FREECAD ASSEMBLY — COMPONENT RECIPES ("column-motor")

This assembly document has 16 components, labeled P0..P15 below (a component is one placed body or linked part). 3 of them carry a construction recipe — the FreeCAD feature program that regenerates the part from scratch, quoted from this document or its linked companion documents; the rest are supplied as boundary geometry only. No exploded tour is included for this assembly.
COMPONENT P0 — recipe-attached ("Semelle", modeled in this document).
Construction recipe (the document's own serialized feature program — sketch geometry with constraints, then the solid features built on it; lengths are millimeters unless a unit is written):

FEATURE [Sketcher::SketchObject] Sketch032
  ArcFitTolerance = 0
  ExternalBSplineMaxDegree = 0
  ExternalBSplineTolerance = 0
  FixShape = 1
  FullyConstrained = true
  InternalTolerance = 1e-06
  InvalidShape = false
  MakeInternals = false
  MapMode = 5
  TreeRank = 0
  ValidateShape = false
  sketch-geometry (56):
    g0: LineSegment StartX=-126.423 StartY=-21.0289 StartZ=0 EndX=-58.007 EndY=18.4711 EndZ=0
    g1: LineSegment StartX=-58.007 StartY=18.4711 StartZ=0 EndX=-45 EndY=41 EndZ=0
    g2: LineSegment StartX=-45 StartY=41 StartZ=0 EndX=-45 EndY=120 EndZ=0
    g3: LineSegment StartX=-45 StartY=120 StartZ=0 EndX=45 EndY=120 EndZ=0
    g4: LineSegment StartX=45 StartY=120 StartZ=0 EndX=45 EndY=41 EndZ=0
    g5: LineSegment StartX=45 StartY=41 StartZ=0 EndX=58.007 EndY=18.4711 EndZ=0
    g6: LineSegment StartX=58.007 StartY=18.4711 StartZ=0 EndX=126.423 EndY=-21.0289 EndZ=0
    g7: LineSegment StartX=126.423 StartY=-21.0289 StartZ=0 EndX=81.423 EndY=-98.9711 EndZ=0
    g8: LineSegment StartX=81.423 StartY=-98.9711 StartZ=0 EndX=13.007 EndY=-59.4711 EndZ=0
    g9: LineSegment StartX=13.007 StartY=-59.4711 StartZ=0 EndX=-13.007 EndY=-59.4711 EndZ=0
    g10: LineSegment StartX=-13.007 StartY=-59.4711 StartZ=0 EndX=-81.423 EndY=-98.9711 EndZ=0
    g11: LineSegment StartX=-81.423 StartY=-98.9711 StartZ=0 EndX=-126.423 EndY=-21.0289 EndZ=0
    g12: LineSegment [constr] StartX=0 StartY=0 StartZ=0 EndX=0 EndY=120 EndZ=0
    g13: LineSegment [constr] StartX=0 StartY=0 StartZ=0 EndX=-103.923 EndY=-60 EndZ=0
    g14: LineSegment [constr] StartX=0 StartY=0 StartZ=0 EndX=103.923 EndY=-60 EndZ=0
    g15: LineSegment StartX=-27.5 StartY=82 StartZ=0 EndX=27.5 EndY=82 EndZ=0
    g16: LineSegment StartX=27.5 StartY=82 StartZ=0 EndX=27.5 EndY=110 EndZ=0
    g17: LineSegment StartX=27.5 StartY=110 StartZ=0 EndX=-27.5 EndY=110 EndZ=0
    g18: LineSegment StartX=-27.5 StartY=110 StartZ=0 EndX=-27.5 EndY=82 EndZ=0
    g19: LineSegment StartX=57.2641 StartY=-64.8157 StartZ=0 EndX=84.7641 EndY=-17.1843 EndZ=0
    g20: LineSegment StartX=84.7641 StartY=-17.1843 StartZ=0 EndX=109.013 EndY=-31.1843 EndZ=0
    g21: LineSegment StartX=109.013 StartY=-31.1843 StartZ=0 EndX=81.5128 EndY=-78.8157 EndZ=0
    g22: LineSegment StartX=81.5128 StartY=-78.8157 StartZ=0 EndX=57.2641 EndY=-64.8157 EndZ=0
    g23: LineSegment StartX=-109.013 StartY=-31.1843 StartZ=0 EndX=-81.5128 EndY=-78.8157 EndZ=0
    g24: LineSegment StartX=-81.5128 StartY=-78.8157 StartZ=0 EndX=-57.2641 EndY=-64.8157 EndZ=0
    g25: LineSegment StartX=-57.2641 StartY=-64.8157 StartZ=0 EndX=-84.7641 EndY=-17.1843 EndZ=0
    g26: LineSegment StartX=-84.7641 StartY=-17.1843 StartZ=0 EndX=-109.013 EndY=-31.1843 EndZ=0
    g27: Circle [constr] CenterX=0 CenterY=0 CenterZ=0 NormalX=0 NormalY=0 NormalZ=1 AngleXU=0 Radius=86.4884
    g28: LineSegment StartX=-11.547 StartY=-20 StartZ=0 EndX=-23.094 EndY=-3.6e-15 EndZ=0
    g29: LineSegment StartX=-23.094 StartY=-3.3e-15 StartZ=0 EndX=-11.547 EndY=20 EndZ=0
    g30: LineSegment StartX=-11.547 StartY=20 StartZ=0 EndX=11.547 EndY=20 EndZ=0
    g31: LineSegment StartX=11.547 StartY=20 StartZ=0 EndX=23.094 EndY=0 EndZ=0
    g32: LineSegment StartX=23.094 StartY=0 StartZ=0 EndX=11.547 EndY=-20 EndZ=0
    g33: LineSegment StartX=11.547 StartY=-20 StartZ=0 EndX=-11.547 EndY=-20 EndZ=0
    g34: Circle [constr] CenterX=0 CenterY=0 CenterZ=0 NormalX=0 NormalY=0 NormalZ=1 AngleXU=0 Radius=23.094
    g35: Circle CenterX=-21.6506 CenterY=12.5 CenterZ=0 NormalX=0 NormalY=0 NormalZ=1 AngleXU=0 Radius=1.6
    g36: Circle CenterX=21.6506 CenterY=12.5 CenterZ=0 NormalX=0 NormalY=0 NormalZ=1 AngleXU=0 Radius=1.6
    g37: Circle CenterX=0 CenterY=-25 CenterZ=0 NormalX=0 NormalY=0 NormalZ=1 AngleXU=0 Radius=1.6
    g38: LineSegment [constr] StartX=0 StartY=-25 StartZ=0 EndX=0 EndY=0 EndZ=0
    g39: LineSegment [constr] StartX=0 StartY=0 StartZ=0 EndX=21.6506 EndY=12.5 EndZ=0
    g40: LineSegment [constr] StartX=0 StartY=0 StartZ=0 EndX=-21.6506 EndY=12.5 EndZ=0
    g41: LineSegment [constr] StartX=-45 StartY=120 StartZ=0 EndX=-126.423 EndY=-21.0289 EndZ=0
    g42: LineSegment [constr] StartX=-81.423 StartY=-98.9711 StartZ=0 EndX=81.423 EndY=-98.9711 EndZ=0
    g43: LineSegment [constr] StartX=126.423 StartY=-21.0289 StartZ=0 EndX=45 EndY=120 EndZ=0
    g44: LineSegment [constr] StartX=-45 StartY=120 StartZ=0 EndX=-55 EndY=102.679 EndZ=0
    g45: LineSegment [constr] StartX=-55 StartY=102.679 StartZ=0 EndX=-45 EndY=41 EndZ=0
    g46: LineSegment [constr] StartX=-58.007 StartY=18.4711 StartZ=0 EndX=-116.423 EndY=-3.70835 EndZ=0
    g47: LineSegment [constr] StartX=-116.423 StartY=-3.70835 StartZ=0 EndX=-126.423 EndY=-21.0289 EndZ=0
    g48: LineSegment [constr] StartX=-81.423 StartY=-98.9711 StartZ=0 EndX=-61.423 EndY=-98.9711 EndZ=0
    g49: LineSegment [constr] StartX=-61.423 StartY=-98.9711 StartZ=0 EndX=-13.007 EndY=-59.4711 EndZ=0
    g50: LineSegment [constr] StartX=13.007 StartY=-59.4711 StartZ=0 EndX=61.423 EndY=-98.9711 EndZ=0
    g51: LineSegment [constr] StartX=61.423 StartY=-98.9711 StartZ=0 EndX=81.423 EndY=-98.9711 EndZ=0
    g52: LineSegment [constr] StartX=126.423 StartY=-21.0289 StartZ=0 EndX=116.423 EndY=-3.70835 EndZ=0
    g53: LineSegment [constr] StartX=116.423 StartY=-3.70835 StartZ=0 EndX=58.007 EndY=18.4711 EndZ=0
    g54: LineSegment [constr] StartX=45 StartY=41 StartZ=0 EndX=55 EndY=102.679 EndZ=0
    g55: LineSegment [constr] StartX=55 StartY=102.679 StartZ=0 EndX=45 EndY=120 EndZ=0
  constraints (151):
    c: Coincident(g0,g1)
    c: Coincident(g1,g2)
    c: Vertical(g2)
    c: Coincident(g2,g3)
    c: Horizontal(g3)
    c: Coincident(g3,g4)
    c: Vertical(g4)
    c: Coincident(g4,g5)
    c: Coincident(g5,g6)
    c: Coincident(g6,g7)
    c: Coincident(g7,g8)
    c: Coincident(g8,g9)
    c: Horizontal(g9)
    c: Coincident(g9,g10)
    c: Coincident(g10,g11)
    c: Coincident(g11,g0)
    c: Parallel(g8,g6)
    c: Parallel(g10,g0)
    c: Equal(g4,g6)
    c: Equal(g6,g8)
    c: Equal(g8,g10)
    c: Equal(g10,g0)
    c: Equal(g0,g2)
    c: Perpendicular(g6,g7)
    c: Perpendicular(g11,g10)
    c: Coincident(g12,g-1)
    c: PointOnObject(g12,g3)
    c: Vertical(g12)
    c: Coincident(g13,g12)
    c: Coincident(g14,g12)
    c: Symmetric(g6,g7,g14)
    c: Symmetric(g10,g0,g13)
    c: Perpendicular(g13,g11)
    c: Perpendicular(g7,g14)
    c: DistanceX(g3,g3) = 90
    c: Equal(g9,g5)
    c: Equal(g5,g1)
    c: Angle(g14,g12) = 2.0944
    c: Angle(g12,g13) = 2.0944
    c: DistanceY(g12,g2) = 120
    c: DistanceX(g9,g9) = 26.0141
    c: Coincident(g15,g16)
    c: Coincident(g16,g17)
    c: Coincident(g17,g18)
    c: Coincident(g18,g15)
    c: Horizontal(g15)
    c: Vertical(g16)
    c: Vertical(g18)
    c: Symmetric(g16,g17,g12)
    c: DistanceX(g17,g17) = 55
    c: DistanceY(g16,g16) = 28
    c: Coincident(g19,g20)
    c: Coincident(g20,g21)
    c: Coincident(g21,g22)
    c: Coincident(g22,g19)
    c: Coincident(g23,g24)
    c: Coincident(g24,g25)
    c: Coincident(g25,g26)
    c: Coincident(g26,g23)
    c: Equal(g25,g23)
    c: Equal(g23,g19)
    c: Equal(g19,g21)
    c: Equal(g21,g15)
    c: Equal(g22,g20)
    c: Equal(g20,g16)
    c: Equal(g16,g26)
    c: Equal(g26,g24)
    c: Parallel(g24,g13)
    c: Parallel(g22,g14)
    c: Symmetric(g23,g23,g13)
    c: Symmetric(g21,g20,g14)
    c: Coincident(g27,g12)
    c: PointOnObject(g19,g27)
    c: PointOnObject(g24,g27)
    c: PointOnObject(g15,g27)
    c: Equal(g11,g7)
    c: Equal(g7,g3)
    c: Coincident(g28,g29)
    c: Coincident(g29,g30)
    c: Coincident(g30,g31)
    c: Coincident(g31,g32)
    c: Coincident(g32,g33)
    c: Coincident(g33,g28)
    c: Horizontal(g33)
    c: Horizontal(g30)
    c: Equal(g29,g30)
    c: Equal(g30,g31)
    c: Equal(g31,g32)
    c: Equal(g32,g33)
    c: Equal(g33,g28)
    c: Coincident(g34,g12)
    c: PointOnObject(g30,g34)
    c: PointOnObject(g31,g34)
    c: PointOnObject(g32,g34)
    c: PointOnObject(g28,g34)
    c: PointOnObject(g28,g34)
    c: DistanceY(g12,g30) = 20
    c: PointOnObject(g37,g-2)
    c: Equal(g37,g36)
    c: Equal(g36,g35)
    c: Diameter(g35) = 3.2
    c: Coincident(g38,g37)
    c: Coincident(g38,g12)
    c: Coincident(g39,g12)
    c: Coincident(g39,g36)
    c: Coincident(g40,g12)
    c: Coincident(g40,g35)
    c: Perpendicular(g29,g40)
    c: Perpendicular(g31,g39)
    c: Equal(g40,g38)
    c: Equal(g38,g39)
    c: DistanceY(g38,g38) = 25
    c: Coincident(g41,g3)
    c: Coincident(g41,g11)
    c: Coincident(g42,g11)
    c: Coincident(g42,g7)
    c: Coincident(g43,g7)
    c: Coincident(g43,g3)
    c: Coincident(g3,g44)
    c: PointOnObject(g44,g41)
    c: Coincident(g44,g45)
    c: Coincident(g45,g1)
    c: Coincident(g1,g46)
    c: PointOnObject(g46,g41)
    c: Coincident(g46,g47)
    c: Coincident(g47,g11)
    c: Coincident(g11,g48)
    c: Horizontal(g48)
    c: Coincident(g48,g49)
    c: Coincident(g49,g9)
    c: Coincident(g9,g50)
    c: PointOnObject(g50,g42)
    c: Coincident(g50,g51)
    c: Coincident(g51,g7)
    c: Coincident(g7,g52)
    c: PointOnObject(g52,g43)
    c: Coincident(g52,g53)
    c: Coincident(g53,g5)
    c: Coincident(g5,g54)
    c: PointOnObject(g54,g43)
    c: Coincident(g54,g55)
    c: Coincident(g55,g3)
    c: Equal(g55,g44)
    c: Equal(g44,g47)
    c: Equal(g47,g48)
    c: Equal(g48,g51)
    c: Equal(g55,g52)
    c: DistanceX(g48,g48) = 20
    c: DistanceY(g16) = 110
    c: DistanceY(g50,g12) = 98.9711
    c: DistanceY(g4,g4) = 79
FEATURE [PartDesign::Pad] Pad020
  AddSubType = 0
  AutoTaperInnerAngle = true
  CheckUpToFaceLimits = true
  ClaimChildren = false
  Direction = (0,0,1)
  Fit = 0
  FitJoin = 0
  FixShape = 1
  InnerFit = 0
  InnerFitJoin = 0
  InvalidShape = false
  Length = 5
  Length2 = 100
  NewSolid = false
  Profile = -> Sketch032
  Refine = true
  Reversed = true
  Suppress = false
  TaperInnerAngle = 0
  TaperInnerAngleRev = 0
  TreeRank = 0
  Type = 0
  ValidateShape = true
  _ProfileBasedVersion = 0
FEATURE [PartDesign::Fillet] Fillet008
  AddSubType = 0
  Base = -> Pad020 [Edge41,Edge44,Edge37,Edge38,Edge65,Edge62,Edge61,Edge68,Edge49,Edge50,Edge53,Edge56]
  BaseFeature = -> Pad020
  FixShape = 1
  InvalidShape = false
  NewSolid = false
  Radius = 3
  Refine = true
  SupportTransform = false
  Suppress = false
  TreeRank = 0
  UseAllEdges = false
  ValidateShape = true
FEATURE [PartDesign::Fillet] Fillet009
  AddSubType = 0
  Base = -> Fillet008 [Edge110,Edge99,Edge107,Edge106,Edge102,Edge103]
  BaseFeature = -> Fillet008
  FixShape = 1
  InvalidShape = false
  NewSolid = false
  Radius = 5
  Refine = true
  SupportTransform = false
  Suppress = false
  TreeRank = 0
  UseAllEdges = false
  ValidateShape = true
FEATURE [PartDesign::Fillet] Fillet010
  AddSubType = 0
  Base = -> Fillet009 [Edge53,Edge57,Edge67,Edge71,Edge77,Edge81]
  BaseFeature = -> Fillet009
  FixShape = 1
  InvalidShape = false
  NewSolid = false
  Radius = 5
  Refine = true
  SupportTransform = false
  Suppress = false
  TreeRank = 0
  UseAllEdges = false
  ValidateShape = true
FEATURE [Sketcher::SketchObject] Sketch033
  ArcFitTolerance = 0
  ExternalBSplineMaxDegree = 0
  ExternalBSplineTolerance = 0
  FixShape = 1
  FullyConstrained = true
  InternalTolerance = 1e-06
  InvalidShape = false
  MakeInternals = false
  MapMode = 5
  TreeRank = 0
  ValidateShape = false
  sketch-geometry (17):
    g0: Circle CenterX=-20 CenterY=115 CenterZ=0 NormalX=0 NormalY=0 NormalZ=1 AngleXU=0 Radius=1.75
    g1: Circle CenterX=20 CenterY=115 CenterZ=0 NormalX=0 NormalY=0 NormalZ=1 AngleXU=0 Radius=1.75
    g2: Circle CenterX=-35 CenterY=60 CenterZ=0 NormalX=0 NormalY=0 NormalZ=1 AngleXU=0 Radius=1.75
    g3: Circle CenterX=-35 CenterY=100 CenterZ=0 NormalX=0 NormalY=0 NormalZ=1 AngleXU=0 Radius=1.75
    g4: Circle CenterX=35 CenterY=100 CenterZ=0 NormalX=0 NormalY=0 NormalZ=1 AngleXU=0 Radius=1.75
    g5: Circle CenterX=35 CenterY=60 CenterZ=0 NormalX=0 NormalY=0 NormalZ=1 AngleXU=0 Radius=1.75
    g6: Circle CenterX=-35 CenterY=115 CenterZ=0 NormalX=0 NormalY=0 NormalZ=1 AngleXU=0 Radius=3.1
    g7: Circle CenterX=35 CenterY=115 CenterZ=0 NormalX=0 NormalY=0 NormalZ=1 AngleXU=0 Radius=3.1
    g8: Circle CenterX=-35 CenterY=80 CenterZ=0 NormalX=0 NormalY=0 NormalZ=1 AngleXU=0 Radius=2.2
    g9: Circle CenterX=35 CenterY=80 CenterZ=0 NormalX=0 NormalY=0 NormalZ=1 AngleXU=0 Radius=2.2
    g10: Circle CenterX=-35 CenterY=50 CenterZ=0 NormalX=0 NormalY=0 NormalZ=1 AngleXU=0 Radius=2.2
    g11: Circle CenterX=35 CenterY=50 CenterZ=0 NormalX=0 NormalY=0 NormalZ=1 AngleXU=0 Radius=2.2
    g12: Circle CenterX=-1.4e-15 CenterY=115 CenterZ=0 NormalX=0 NormalY=0 NormalZ=1 AngleXU=0 Radius=2.2
    g13: Circle CenterX=-25.75 CenterY=76 CenterZ=0 NormalX=0 NormalY=0 NormalZ=1 AngleXU=0 Radius=1.75
    g14: Circle CenterX=-25.75 CenterY=55 CenterZ=0 NormalX=0 NormalY=0 NormalZ=1 AngleXU=0 Radius=1.75
    g15: Circle CenterX=25.75 CenterY=76 CenterZ=0 NormalX=0 NormalY=0 NormalZ=1 AngleXU=0 Radius=1.75
    g16: Circle CenterX=25.75 CenterY=55 CenterZ=0 NormalX=0 NormalY=0 NormalZ=1 AngleXU=0 Radius=1.75
  constraints (41):
    c: Equal(g0,g3)
    c: Equal(g3,g2)
    c: Equal(g2,g1)
    c: Equal(g1,g4)
    c: Equal(g4,g5)
    c: Diameter(g0) = 3.5
    c: Symmetric(g1,g0,g-2)
    c: Symmetric(g3,g4,g-2)
    c: Symmetric(g2,g5,g-2)
    c: Vertical(g3,g2)
    c: DistanceX(g3,g4) = 70
    c: DistanceX(g0,g1) = 40
    c: DistanceY(g4,g1) = 15
    c: DistanceY(g5,g4) = 40
    c: DistanceY(g-1,g1) = 115
    c: Symmetric(g7,g6,g-2)
    c: Horizontal(g6,g0)
    c: Diameter(g7) = 6.2
    c: Equal(g7,g6)
    c: Vertical(g7,g4)
    c: Equal(g9,g8)
    c: Symmetric(g8,g9,g-2)
    c: Symmetric(g5,g4,g9)
    c: Diameter(g9) = 4.4
    c: Symmetric(g1,g0,g12)
    c: Equal(g12,g11)
    c: Equal(g11,g10)
    c: Equal(g10,g9)
    c: Vertical(g11,g5)
    c: Symmetric(g11,g10,g-2)
    c: DistanceY(g11,g5) = 10
    c: Equal(g15,g16)
    c: Equal(g16,g14)
    c: Equal(g14,g13)
    c: Equal(g13,g2)
    c: Vertical(g13,g14)
    c: Symmetric(g15,g13,g-2)
    c: Symmetric(g14,g16,g-2)
    c: DistanceX(g8,g13) = 9.25
    c: DistanceY(g-1,g13) = 76
    c: DistanceY(g14,g13) = 21
FEATURE [PartDesign::Pocket] Pocket012
  AddSubType = 1
  AutoTaperInnerAngle = true
  BaseFeature = -> Fillet010
  CheckUpToFaceLimits = true
  ClaimChildren = false
  Direction = (0,0,-1)
  Fit = 0
  FitJoin = 0
  FixShape = 1
  InnerFit = 0
  InnerFitJoin = 0
  InvalidShape = false
  Length = 5
  Length2 = 100
  NewSolid = false
  Profile = -> Sketch033
  Refine = true
  Suppress = false
  TaperInnerAngle = 0
  TaperInnerAngleRev = 0
  TreeRank = 0
  Type = 1
  ValidateShape = true
  _ProfileBasedVersion = 0
  _Version = 0
FEATURE [PartDesign::PolarPattern] PolarPattern013
  AddSubType = 0
  Angle = 360
  Axis = -> Sketch033 [N_Axis]
  BaseFeature = -> Pocket012
  CopyShape = true
  FixShape = 1
  HideBaseFeature = false
  InvalidShape = false
  NewSolid = false
  Occurrences = 3
  OffsetBaseFeature = true
  OriginalSubs = -> [Pocket012]
  Originals = -> [Pocket012]
  ParallelTransform = true
  Refine = true
  SubTransform = true
  Suppress = false
  TreeRank = 0
  ValidateShape = true
  _Version = 0
FEATURE [Sketcher::SketchObject] Sketch034
  ArcFitTolerance = 0
  ExternalBSplineMaxDegree = 0
  ExternalBSplineTolerance = 0
  ExternalGeometry = -> [PolarPattern013]
  FixShape = 1
  FullyConstrained = true
  InternalTolerance = 1e-06
  InvalidShape = false
  MakeInternals = false
  MapMode = 5
  TreeRank = 0
  ValidateShape = false
  sketch-geometry (5):
    g0: LineSegment StartX=-21.5 StartY=20 StartZ=0 EndX=21.5 EndY=20 EndZ=0
    g1: LineSegment StartX=21.5 StartY=20 StartZ=0 EndX=21.5 EndY=82 EndZ=0
    g2: LineSegment StartX=21.5 StartY=82 StartZ=0 EndX=-21.5 EndY=82 EndZ=0
    g3: LineSegment StartX=-21.5 StartY=82 StartZ=0 EndX=-21.5 EndY=20 EndZ=0
    g4: GeomPoint [constr] X=0 Y=51 Z=0
  constraints (13):
    c: Coincident(g0,g1)
    c: Coincident(g1,g2)
    c: Coincident(g2,g3)
    c: Coincident(g3,g0)
    c: Horizontal(g0)
    c: Horizontal(g2)
    c: Vertical(g1)
    c: Vertical(g3)
    c: Symmetric(g2,g0,g4)
    c: PointOnObject(g4,g-2)
    c: Distance(g2,g2) = 43
    c: PointOnObject(g-4,g0)
    c: PointOnObject(g1,g-3)
FEATURE [PartDesign::Pocket] Pocket
  AddSubType = 1
  AutoTaperInnerAngle = true
  BaseFeature = -> PolarPattern013
  CheckUpToFaceLimits = true
  ClaimChildren = false
  Direction = (0,0,-1)
  Fit = 0
  FitJoin = 0
  FixShape = 1
  InnerFit = 0
  InnerFitJoin = 0
  InvalidShape = false
  Length = 5
  Length2 = 5
  NewSolid = false
  Profile = -> Sketch034
  ReferenceAxis = -> Sketch034 [N_Axis]
  Refine = true
  Suppress = false
  TaperInnerAngle = 0
  TaperInnerAngleRev = 0
  TreeRank = 0
  Type = 1
  ValidateShape = true
  _ProfileBasedVersion = 0
  _Version = 0
FEATURE [PartDesign::PolarPattern] PolarPattern
  AddSubType = 0
  Angle = 360
  Axis = -> Z_Axis026
  BaseFeature = -> Pocket
  CopyShape = true
  FixShape = 1
  HideBaseFeature = false
  InvalidShape = false
  NewSolid = false
  Occurrences = 3
  OffsetBaseFeature = true
  OriginalSubs = -> [Pocket]
  Originals = -> [Pocket]
  ParallelTransform = true
  Refine = true
  SubTransform = true
  Suppress = false
  TreeRank = 0
  ValidateShape = true
  _Version = 0
FEATURE [PartDesign::Fillet] Fillet011
  AddSubType = 0
  Base = -> PolarPattern [Edge284,Edge302,Edge340,Edge275,Edge312,Edge330,Edge334,Edge336,Edge278,Edge280,Edge306,Edge308]
  BaseFeature = -> PolarPattern
  FixShape = 1
  InvalidShape = false
  NewSolid = false
  Radius = 2
  Refine = true
  SupportTransform = false
  Suppress = false
  TreeRank = 0
  UseAllEdges = false
  ValidateShape = true
FEATURE [PartDesign::Body] Body019  label="Semelle"
  AutoGroupSolids = false
  ClaimAllChildren = false
  ExportMode = 0
  FixShape = 1
  Group = -> [Sketch032,Pad020,Fillet008,Fillet009,Fillet010,Sketch033,Pocket012,PolarPattern013,Sketch034,Pocket,PolarPattern,Fillet011]
  InvalidShape = false
  Origin = -> Origin029
  SingleSolid = true
  Tip = -> Fillet011
  TreeRank = 0
  ValidateShape = false
  _ExportChildren = -> [Pad020,Fillet008,Fillet009,Fillet010,Pocket012,PolarPattern013,Pocket,PolarPattern,Fillet011]
  _GroupVersion = 1
COMPONENT P1 — recipe-attached ("Side_A", modeled in this document).
Construction recipe (the document's own serialized feature program — sketch geometry with constraints, then the solid features built on it; lengths are millimeters unless a unit is written):

FEATURE [Sketcher::SketchObject] Sketch136
  ArcFitTolerance = 1e-06
  AttachmentSupport = -> [YZ_Plane085]
  ExternalBSplineMaxDegree = 5
  ExternalBSplineTolerance = 0.0001
  FullyConstrained = true
  InternalTolerance = 1e-06
  InvalidShape = false
  MakeInternals = false
  MapMode = 5
  Placement = pos=(0,0,0) rot=(0.57735,0.57735,0.57735;2.0944rad)
  Support = -> [YZ_Plane085]
  TreeRank = 1041
  ValidateShape = false
  sketch-geometry (4):
    g0: LineSegment StartX=73.73 StartY=0 StartZ=0 EndX=0 EndY=0 EndZ=0
    g1: LineSegment StartX=0 StartY=0 StartZ=0 EndX=0 EndY=255.6 EndZ=0
    g2: LineSegment StartX=0 StartY=255.6 StartZ=0 EndX=28.2254 EndY=258.069 EndZ=0
    g3: LineSegment StartX=28.2254 StartY=258.069 StartZ=0 EndX=73.73 EndY=0 EndZ=0
  constraints (11):
    c: PointOnObject(g0,g-1)
    c: Coincident(g0,g-1)
    c: Coincident(g0,g1)
    c: Vertical(g1)
    c: Coincident(g1,g2)
    c: Coincident(g2,g3)
    c: Coincident(g3,g0)
    c: Angle(g3,g0) = 1.39626
    c: DistanceX(g0,g0) = 73.73
    c: Angle(g1,g2) = 1.65806
    c: DistanceY(g1,g1) = 255.6
FEATURE [PartDesign::Pad] Pad069
  AddSubType = 0
  AlongSketchNormal = false
  AutoTaperInnerAngle = true
  CheckUpToFaceLimits = true
  ClaimChildren = false
  Direction = (1,-2e-16,3e-16)
  Fit = 0
  FitJoin = 0
  InnerFit = 0
  InnerFitJoin = 0
  InvalidShape = false
  Length = 3
  Length2 = 10
  Linearize = true
  NewSolid = false
  Profile = -> Sketch136
  ReferenceAxis = -> Sketch136 [N_Axis]
  Refine = true
  Reversed = true
  Suppress = false
  TaperInnerAngle = 0
  TaperInnerAngleRev = 0
  TreeRank = 1042
  Type = 0
  ValidateShape = true
  _ProfileBasedVersion = 1
FEATURE [Sketcher::SketchObject] Sketch137
  ArcFitTolerance = 1e-06
  AttachmentSupport = -> [YZ_Plane085]
  ExternalBSplineMaxDegree = 5
  ExternalBSplineTolerance = 0.0001
  FullyConstrained = true
  InternalTolerance = 1e-06
  InvalidShape = false
  MakeInternals = false
  MapMode = 5
  Placement = pos=(0,0,0) rot=(0.57735,0.57735,0.57735;2.0944rad)
  Support = -> [YZ_Plane085]
  TreeRank = 1043
  ValidateShape = false
  sketch-geometry (12):
    g0: LineSegment StartX=0 StartY=0 StartZ=0 EndX=10 EndY=0 EndZ=0
    g1: LineSegment StartX=10 StartY=0 StartZ=0 EndX=10 EndY=21 EndZ=0
    g2: LineSegment StartX=10 StartY=21 StartZ=0 EndX=0 EndY=21 EndZ=0
    g3: LineSegment StartX=0 StartY=21 StartZ=0 EndX=0 EndY=0 EndZ=0
    g4: LineSegment StartX=0 StartY=79 StartZ=0 EndX=10 EndY=79 EndZ=0
    g5: LineSegment StartX=10 StartY=79 StartZ=0 EndX=10 EndY=101 EndZ=0
    g6: LineSegment StartX=10 StartY=101 StartZ=0 EndX=0 EndY=101 EndZ=0
    g7: LineSegment StartX=0 StartY=101 StartZ=0 EndX=0 EndY=79 EndZ=0
    g8: LineSegment StartX=0 StartY=159 StartZ=0 EndX=10 EndY=159 EndZ=0
    g9: LineSegment StartX=10 StartY=159 StartZ=0 EndX=10 EndY=181 EndZ=0
    g10: LineSegment StartX=10 StartY=181 StartZ=0 EndX=0 EndY=181 EndZ=0
    g11: LineSegment StartX=0 StartY=181 StartZ=0 EndX=0 EndY=159 EndZ=0
  constraints (35):
    c: Coincident(g0,g1)
    c: Coincident(g1,g2)
    c: Coincident(g2,g3)
    c: Coincident(g3,g0)
    c: Horizontal(g0)
    c: Horizontal(g2)
    c: Vertical(g1)
    c: Vertical(g3)
    c: Coincident(g0,g-1)
    c: DistanceY(g3,g3) = 21
    c: DistanceX(g2,g2) = 10
    c: Coincident(g4,g5)
    c: Coincident(g5,g6)
    c: Coincident(g6,g7)
    c: Coincident(g7,g4)
    c: Horizontal(g4)
    c: Horizontal(g6)
    c: Vertical(g5)
    c: Vertical(g7)
    c: PointOnObject(g4,g-2)
    c: Coincident(g8,g9)
    c: Coincident(g9,g10)
    c: Coincident(g10,g11)
    c: Coincident(g11,g8)
    c: Horizontal(g8)
    c: Horizontal(g10)
    c: Vertical(g9)
    c: Vertical(g11)
    c: PointOnObject(g8,g-2)
    c: Equal(g2,g4)
    c: Equal(g4,g8)
    c: DistanceY(g2,g4) = 58
    c: DistanceY(g6,g8) = 58
    c: DistanceY(g5,g5) = 22
    c: DistanceY(g9,g9) = 22
FEATURE [PartDesign::Pocket] Pocket067
  AddSubType = 1
  AlongSketchNormal = false
  AutoTaperInnerAngle = true
  BaseFeature = -> Pad069
  CheckUpToFaceLimits = true
  ClaimChildren = false
  Direction = (-1,2e-16,-3e-16)
  Fit = 0
  FitJoin = 0
  InnerFit = 0
  InnerFitJoin = 0
  InvalidShape = false
  Length = 5
  Length2 = 10
  Linearize = true
  NewSolid = false
  Profile = -> Sketch137
  ReferenceAxis = -> Sketch137 [N_Axis]
  Refine = true
  Suppress = false
  TaperInnerAngle = 0
  TaperInnerAngleRev = 0
  TreeRank = 1044
  Type = 0
  ValidateShape = true
  _ProfileBasedVersion = 1
  _Version = 1
FEATURE [PartDesign::Chamfer] Chamfer056
  AddSubType = 0
  Angle = 45
  Base = -> Pocket067 [Edge41,Edge40,Edge39,Edge38,Edge36,Edge37,Edge34,Edge35,Edge18,Edge33]
  BaseFeature = -> Pocket067
  ChamferType = 0
  FlipDirection = false
  InvalidShape = false
  NewSolid = false
  Refine = true
  Size = 1
  Size2 = 1
  SupportTransform = false
  Suppress = false
  TreeRank = 1045
  UseAllEdges = false
  ValidateShape = true
FEATURE [Sketcher::SketchObject] Sketch138
  ArcFitTolerance = 1e-06
  AttachmentSupport = -> [YZ_Plane085]
  ExternalBSplineMaxDegree = 5
  ExternalBSplineTolerance = 0.0001
  ExternalGeometry = -> [Chamfer056]
  FullyConstrained = true
  InternalTolerance = 1e-06
  InvalidShape = false
  MakeInternals = false
  MapMode = 5
  Placement = pos=(0,0,0) rot=(0.57735,0.57735,0.57735;2.0944rad)
  Support = -> [YZ_Plane085]
  TreeRank = 1046
  ValidateShape = false
  sketch-geometry (15):
    g0: ArcOfCircle CenterX=-0.662278 CenterY=190 CenterZ=0 NormalX=0 NormalY=0 NormalZ=1 AngleXU=0 Radius=3 StartAngle=1.3482 EndAngle=4.93498
    g1: ArcOfCircle CenterX=5 CenterY=190 CenterZ=0 NormalX=0 NormalY=0 NormalZ=1 AngleXU=0 Radius=1.75 StartAngle=4.93498 EndAngle=7.63139
    g2: LineSegment StartX=-4.22e-14 StartY=187.074 StartZ=0 EndX=5.38633 EndY=188.293 EndZ=0
    g3: LineSegment StartX=5.38633 StartY=191.707 StartZ=0 EndX=-4.26e-14 EndY=192.926 EndZ=0
    g4: ArcOfCircle CenterX=71.7775 CenterY=14.8871 CenterZ=0 NormalX=0 NormalY=0 NormalZ=1 AngleXU=0 Radius=3 StartAngle=4.66433 EndAngle=8.25111
    g5: ArcOfCircle CenterX=66.2012 CenterY=13.9039 CenterZ=0 NormalX=0 NormalY=0 NormalZ=1 AngleXU=0 Radius=1.75 StartAngle=1.96792 EndAngle=4.66433
    g6: LineSegment StartX=70.6172 StartY=17.6536 StartZ=0 EndX=65.5244 EndY=15.5177 EndZ=0
    g7: LineSegment StartX=66.1172 StartY=12.1559 StartZ=0 EndX=71.6334 EndY=11.8906 EndZ=0
    g8: LineSegment [constr] StartX=66.2012 StartY=13.9039 StartZ=0 EndX=71.1253 EndY=14.7721 EndZ=0
    g9: ArcOfCircle CenterX=60.4904 CenterY=78.8996 CenterZ=0 NormalX=0 NormalY=0 NormalZ=1 AngleXU=0 Radius=3 StartAngle=4.66433 EndAngle=8.25111
    g10: ArcOfCircle CenterX=54.9141 CenterY=77.9164 CenterZ=0 NormalX=0 NormalY=0 NormalZ=1 AngleXU=0 Radius=1.75 StartAngle=1.96792 EndAngle=4.66433
    g11: LineSegment StartX=59.3301 StartY=81.6662 StartZ=0 EndX=54.2373 EndY=79.5302 EndZ=0
    g12: LineSegment StartX=54.83 StartY=76.1684 StartZ=0 EndX=60.3462 EndY=75.9031 EndZ=0
    g13: LineSegment [constr] StartX=54.9141 StartY=77.9164 StartZ=0 EndX=59.8381 EndY=78.7846 EndZ=0
    g14: Circle [constr] CenterX=5 CenterY=190 CenterZ=0 NormalX=0 NormalY=0 NormalZ=1 AngleXU=0 Radius=9
  constraints (38):
    c: Tangent(g0,g2) = -1.5708
    c: Tangent(g2,g1) = -1.5708
    c: Tangent(g1,g3) = -1.5708
    c: Tangent(g3,g0) = -1.5708
    c: Radius(g0) = 3
    c: Radius(g1) = 1.75
    c: Horizontal(g1,g0)
    c: PointOnObject(g0,g-3)
    c: DistanceX(g0,g1) = 5
    c: Tangent(g4,g6) = -1.5708
    c: Tangent(g6,g5) = -1.5708
    c: Tangent(g5,g7) = -1.5708
    c: Tangent(g7,g4) = -1.5708
    c: Equal(g0,g4)
    c: Equal(g5,g1)
    c: PointOnObject(g4,g-4)
    c: PointOnObject(g4,g-4)
    c: Coincident(g8,g5)
    c: PointOnObject(g8,g-4)
    c: Perpendicular(g-4,g8)
    c: Distance(g8) = 5
    c: Distance(g8,g-4) = 15
    c: Tangent(g9,g11) = -1.5708
    c: Tangent(g11,g10) = -1.5708
    c: Tangent(g10,g12) = -1.5708
    c: Tangent(g12,g9) = -1.5708
    c: Equal(g9,g0)
    c: Equal(g10,g1)
    c: PointOnObject(g9,g-4)
    c: PointOnObject(g9,g-4)
    c: Coincident(g13,g10)
    c: PointOnObject(g13,g-4)
    c: Perpendicular(g-4,g13)
    c: Distance(g13) = 5
    c: Distance(g13,g-4) = 80
    c: Coincident(g14,g1)
    c: Diameter(g14) = 18
    c: Tangent(g14,g-5)
FEATURE [PartDesign::Pocket] Pocket068
  AddSubType = 1
  AlongSketchNormal = false
  AutoTaperInnerAngle = true
  BaseFeature = -> Chamfer056
  CheckUpToFaceLimits = true
  ClaimChildren = false
  Direction = (-1,2e-16,-3e-16)
  Fit = 0
  FitJoin = 0
  InnerFit = 0
  InnerFitJoin = 0
  InvalidShape = false
  Length = 5
  Length2 = 10
  Linearize = true
  NewSolid = false
  Profile = -> Sketch138
  ReferenceAxis = -> Sketch138 [N_Axis]
  Refine = true
  Suppress = false
  TaperInnerAngle = 0
  TaperInnerAngleRev = 0
  TreeRank = 1047
  Type = 0
  ValidateShape = true
  _ProfileBasedVersion = 1
  _Version = 1
FEATURE [PartDesign::Chamfer] Chamfer057
  AddSubType = 0
  Angle = 45
  Base = -> Pocket068 [Edge96,Edge102,Edge88,Edge94,Edge82,Edge76]
  BaseFeature = -> Pocket068
  ChamferType = 0
  FlipDirection = false
  InvalidShape = false
  NewSolid = false
  Refine = true
  Size = 1
  Size2 = 1
  SupportTransform = false
  Suppress = false
  TreeRank = 1048
  UseAllEdges = false
  ValidateShape = true
FEATURE [PartDesign::Chamfer] Chamfer058
  AddSubType = 0
  Angle = 45
  Base = -> Chamfer057 [Edge66,Edge70,Edge122,Edge124]
  BaseFeature = -> Chamfer057
  ChamferType = 0
  FlipDirection = false
  InvalidShape = false
  NewSolid = false
  Refine = true
  Size = 3
  Size2 = 1
  SupportTransform = false
  Suppress = false
  TreeRank = 1049
  UseAllEdges = false
  ValidateShape = true
FEATURE [PartDesign::Body] Body052  label="CarterLateral"
  AutoGroupSolids = false
  ClaimAllChildren = false
  ExportMode = 0
  Group = -> [Sketch136,Pad069,Sketch137,Pocket067,Chamfer056,Sketch138,Pocket068,Chamfer057,Chamfer058]
  InvalidShape = false
  Origin = -> Origin102
  Placement = pos=(-40,40,46) rot=(0,0,1;0rad)
  Tip = -> Chamfer058
  TreeRank = 1040
  ValidateShape = false
  _ExportChildren = -> [Pad069,Pocket067,Chamfer056,Pocket068,Chamfer057,Chamfer058]
  _GroupVersion = 1
FEATURE [PartDesign::FeatureBase] Clone001
  BaseFeature = -> Body052
  InvalidShape = false
  NewSolid = false
  Placement = pos=(-40,40,46) rot=(0,0,1;0rad)
  Suppress = false
  TreeRank = 1059
  ValidateShape = true
FEATURE [Sketcher::SketchObject] Sketch139
  ArcFitTolerance = 1e-06
  AttachmentSupport = -> [Clone001]
  ExternalBSplineMaxDegree = 5
  ExternalBSplineTolerance = 0.0001
  ExternalGeometry = -> [Clone001]
  FullyConstrained = true
  InternalTolerance = 1e-06
  InvalidShape = false
  MakeInternals = false
  MapMode = 5
  Placement = pos=(-40,40,46) rot=(0.57735,0.57735,0.57735;2.0944rad)
  Support = -> [Clone001]
  TreeRank = 1061
  ValidateShape = false
  sketch-geometry (4):
    g0: LineSegment StartX=6.39e-14 StartY=197.5 StartZ=0 EndX=38.9054 EndY=197.5 EndZ=0
    g1: LineSegment StartX=38.9054 StartY=197.5 StartZ=0 EndX=38.9054 EndY=267.5 EndZ=0
    g2: LineSegment StartX=38.9054 StartY=267.5 StartZ=0 EndX=6.39e-14 EndY=267.5 EndZ=0
    g3: LineSegment StartX=6.39e-14 StartY=267.5 StartZ=0 EndX=6.39e-14 EndY=197.5 EndZ=0
  constraints (12):
    c: Coincident(g0,g1)
    c: Coincident(g1,g2)
    c: Coincident(g2,g3)
    c: Coincident(g3,g0)
    c: Horizontal(g0)
    c: Horizontal(g2)
    c: Vertical(g1)
    c: Vertical(g3)
    c: PointOnObject(g0,g-3)
    c: PointOnObject(g0,g-4)
    c: DistanceY(g-1,g0) = 197.5
    c: DistanceY(g1,g1) = 70
FEATURE [PartDesign::Pocket] Pocket069
  AddSubType = 1
  AlongSketchNormal = false
  AutoTaperInnerAngle = true
  BaseFeature = -> Clone001
  CheckUpToFaceLimits = true
  ClaimChildren = false
  Direction = (-1,-1e-16,-1e-16)
  Fit = 0
  FitJoin = 0
  InnerFit = 0
  InnerFitJoin = 0
  InvalidShape = false
  Length = 5
  Length2 = 10
  Linearize = true
  NewSolid = false
  Profile = -> Sketch139
  ReferenceAxis = -> Sketch139 [N_Axis]
  Refine = true
  Suppress = false
  TaperInnerAngle = 0
  TaperInnerAngleRev = 0
  TreeRank = 1062
  Type = 0
  ValidateShape = true
  _ProfileBasedVersion = 1
  _Version = 1
FEATURE [PartDesign::Chamfer] Chamfer059
  AddSubType = 0
  Angle = 45
  Base = -> Pocket069 [Edge48,Edge45]
  BaseFeature = -> Pocket069
  ChamferType = 0
  FlipDirection = false
  InvalidShape = false
  NewSolid = false
  Refine = true
  Size = 2
  Size2 = 1
  SupportTransform = false
  Suppress = false
  TreeRank = 1063
  UseAllEdges = false
  ValidateShape = true
FEATURE [PartDesign::Body] Body053  label="CarterLateralServo"
  AutoGroupSolids = false
  BaseFeature = -> Body052
  ClaimAllChildren = false
  ExportMode = 0
  Group = -> [Clone001,Sketch139,Pocket069,Chamfer059]
  InvalidShape = false
  Origin = -> Origin103
  Placement = pos=(83,0,0) rot=(0,0,1;0rad)
  Tip = -> Chamfer059
  TreeRank = 1060
  ValidateShape = false
  _ExportChildren = -> [Clone001,Pocket069,Chamfer059]
  _GroupVersion = 1
FEATURE [Sketcher::SketchObject] Sketch140
  ArcFitTolerance = 1e-06
  AttachmentSupport = -> [YZ_Plane087]
  ExternalBSplineMaxDegree = 5
  ExternalBSplineTolerance = 0.0001
  FullyConstrained = true
  InternalTolerance = 1e-06
  InvalidShape = false
  MakeInternals = false
  MapMode = 5
  Placement = pos=(0,0,0) rot=(0.57735,0.57735,0.57735;2.0944rad)
  Support = -> [YZ_Plane087]
  TreeRank = 1074
  ValidateShape = false
  sketch-geometry (5):
    g0: LineSegment StartX=0 StartY=-5 StartZ=0 EndX=0 EndY=10 EndZ=0
    g1: LineSegment StartX=0 StartY=10 StartZ=0 EndX=-6.34777 EndY=46 EndZ=0
    g2: LineSegment StartX=-6.34777 StartY=46 StartZ=0 EndX=3 EndY=46 EndZ=0
    g3: LineSegment StartX=3 StartY=46 StartZ=0 EndX=3 EndY=-5 EndZ=0
    g4: LineSegment StartX=3 StartY=-5 StartZ=0 EndX=0 EndY=-5 EndZ=0
  constraints (15):
    c: PointOnObject(g0,g-2)
    c: PointOnObject(g0,g-2)
    c: Coincident(g0,g1)
    c: Coincident(g1,g2)
    c: Horizontal(g2)
    c: Coincident(g2,g3)
    c: Vertical(g3)
    c: Coincident(g3,g4)
    c: Coincident(g4,g0)
    c: Horizontal(g4)
    c: DistanceY(g0,g-1) = 5
    c: DistanceY(g0) = 10
    c: Angle(g1,g-2) = 2.96706
    c: DistanceX(g4,g4) = 3
    c: DistanceY(g-1,g2) = 46
FEATURE [PartDesign::Pad] Pad070
  AddSubType = 0
  AlongSketchNormal = false
  AutoTaperInnerAngle = true
  CheckUpToFaceLimits = true
  ClaimChildren = false
  Direction = (1,-2e-16,3e-16)
  Fit = 0
  FitJoin = 0
  InnerFit = 0
  InnerFitJoin = 0
  InvalidShape = false
  Length = 80
  Length2 = 10
  Linearize = true
  Midplane = true
  NewSolid = false
  Profile = -> Sketch140
  ReferenceAxis = -> Sketch140 [N_Axis]
  Refine = true
  Suppress = false
  TaperInnerAngle = 0
  TaperInnerAngleRev = 0
  TreeRank = 1075
  Type = 0
  ValidateShape = true
  _ProfileBasedVersion = 1
FEATURE [Sketcher::SketchObject] Sketch141
  ArcFitTolerance = 1e-06
  AttachmentSupport = -> [Pad070]
  ExternalBSplineMaxDegree = 5
  ExternalBSplineTolerance = 0.0001
  ExternalGeometry = -> [Pad070]
  FullyConstrained = true
  InternalTolerance = 1e-06
  InvalidShape = false
  MakeInternals = false
  MapMode = 5
  Placement = pos=(3e-16,1.7101,0.301537) rot=(1,0,0;1.74533rad)
  Support = -> [Pad070]
  TreeRank = 1076
  ValidateShape = false
  sketch-geometry (3):
    g0: LineSegment [constr] StartX=-40 StartY=46.4034 StartZ=0 EndX=-40 EndY=0 EndZ=0
    g1: Circle CenterX=-35 CenterY=34.4034 CenterZ=0 NormalX=0 NormalY=0 NormalZ=1 AngleXU=0 Radius=1.65
    g2: Circle CenterX=35 CenterY=34.4034 CenterZ=0 NormalX=0 NormalY=0 NormalZ=1 AngleXU=0 Radius=1.65
  constraints (8):
    c: Coincident(g0,g-3)
    c: Vertical(g0)
    c: PointOnObject(g0,g-1)
    c: Equal(g1,g2)
    c: Diameter(g1) = 3.3
    c: DistanceX(g-3,g1) = 5
    c: Symmetric(g1,g2,g-2)
    c: DistanceY(g1,g-3) = 12
FEATURE [PartDesign::Pocket] Pocket070
  AddSubType = 1
  AlongSketchNormal = false
  AutoTaperInnerAngle = true
  BaseFeature = -> Pad070
  CheckUpToFaceLimits = true
  ClaimChildren = false
  Direction = (2e-16,0.984808,0.173648)
  Fit = 0
  FitJoin = 0
  InnerFit = 0
  InnerFitJoin = 0
  InvalidShape = false
  Length = 13
  Length2 = 10
  Linearize = true
  NewSolid = false
  Profile = -> Sketch141
  ReferenceAxis = -> Sketch141 [N_Axis]
  Refine = true
  Suppress = false
  TaperInnerAngle = 0
  TaperInnerAngleRev = 0
  TreeRank = 1077
  Type = 0
  ValidateShape = true
  _ProfileBasedVersion = 1
  _Version = 1
FEATURE [Sketcher::SketchObject] Sketch142
  ArcFitTolerance = 1e-06
  AttachmentOffset = pos=(0,0,-2.5) rot=(0,0,1;0rad)
  AttachmentSupport = -> [Pocket070]
  ExternalBSplineMaxDegree = 5
  ExternalBSplineTolerance = 0.0001
  ExternalGeometry = -> [Pocket070]
  FullyConstrained = true
  InternalTolerance = 1e-06
  InvalidShape = false
  MakeInternals = false
  MapMode = 5
  Placement = pos=(7e-16,4.17212,0.735657) rot=(1,0,0;1.74533rad)
  Support = -> [Pocket070]
  TreeRank = 1078
  ValidateShape = false
  sketch-geometry (4):
    g0: ArcOfCircle CenterX=-35 CenterY=34.4034 CenterZ=0 NormalX=0 NormalY=0 NormalZ=1 AngleXU=0 Radius=4 StartAngle=4.71239 EndAngle=7.85398
    g1: ArcOfCircle CenterX=-40 CenterY=34.4034 CenterZ=0 NormalX=0 NormalY=0 NormalZ=1 AngleXU=0 Radius=4 StartAngle=1.5708 EndAngle=4.71239
    g2: LineSegment StartX=-35 StartY=38.4034 StartZ=0 EndX=-40 EndY=38.4034 EndZ=0
    g3: LineSegment StartX=-40 StartY=30.4034 StartZ=0 EndX=-35 EndY=30.4034 EndZ=0
  constraints (9):
    c: Tangent(g0,g2) = -1.5708
    c: Tangent(g2,g1) = -1.5708
    c: Tangent(g1,g3) = -1.5708
    c: Tangent(g3,g0) = -1.5708
    c: Equal(g0,g1)
    c: Coincident(g0,g-3)
    c: Horizontal(g2)
    c: Vertical(g1,g-5)
    c: Radius(g0) = 4
FEATURE [PartDesign::Pocket] Pocket071
  AddSubType = 1
  AlongSketchNormal = false
  AutoTaperInnerAngle = true
  BaseFeature = -> Pocket070
  CheckUpToFaceLimits = true
  ClaimChildren = false
  Direction = (2e-16,0.984808,0.173648)
  Fit = 0
  FitJoin = 0
  InnerFit = 0
  InnerFitJoin = 0
  InvalidShape = false
  Length = 10
  Length2 = 10
  Linearize = true
  NewSolid = false
  Profile = -> Sketch142
  ReferenceAxis = -> Sketch142 [N_Axis]
  Refine = true
  Suppress = false
  TaperInnerAngle = 0
  TaperInnerAngleRev = 0
  TreeRank = 1079
  Type = 0
  ValidateShape = true
  _ProfileBasedVersion = 1
  _Version = 1
FEATURE [PartDesign::Mirrored] Mirrored011
  AddSubType = 0
  BaseFeature = -> Pocket071
  CopyShape = false
  HideBaseFeature = false
  InvalidShape = false
  MirrorPlane = -> Sketch142 [V_Axis]
  NewSolid = false
  OffsetBaseFeature = true
  OriginalSubs = -> [Pocket071]
  Originals = -> [Pocket071]
  ParallelTransform = true
  Refine = true
  SubTransform = true
  Suppress = false
  TreeRank = 1080
  ValidateShape = true
  _Version = 3
FEATURE [PartDesign::Chamfer] Chamfer060
  AddSubType = 0
  Angle = 45
  Base = -> Mirrored011 [Edge19,Edge13]
  BaseFeature = -> Mirrored011
  ChamferType = 0
  FlipDirection = false
  InvalidShape = false
  NewSolid = false
  Refine = true
  Size = 3
  Size2 = 1
  SupportTransform = false
  Suppress = false
  TreeRank = 1081
  UseAllEdges = false
  ValidateShape = true
FEATURE [PartDesign::Chamfer] Chamfer061
  AddSubType = 0
  Angle = 45
  Base = -> Chamfer060 [Edge26,Edge29,Edge13,Edge16]
  BaseFeature = -> Chamfer060
  ChamferType = 0
  FlipDirection = false
  InvalidShape = false
  NewSolid = false
  Refine = true
  Size = 1
  Size2 = 1
  SupportTransform = false
  Suppress = false
  TreeRank = 1083
  UseAllEdges = false
  ValidateShape = true
FEATURE [PartDesign::Chamfer] Chamfer062
  AddSubType = 0
  Angle = 45
  Base = -> Chamfer061 [Edge67,Edge41,Edge36,Edge42]
  BaseFeature = -> Chamfer061
  ChamferType = 0
  FlipDirection = false
  InvalidShape = false
  NewSolid = false
  Refine = true
  Size = 0.4
  Size2 = 1
  SupportTransform = false
  Suppress = false
  TreeRank = 1084
  UseAllEdges = false
  ValidateShape = true
FEATURE [Sketcher::SketchObject] Sketch143
  ArcFitTolerance = 1e-06
  AttachmentSupport = -> [XZ_Plane087]
  ExternalBSplineMaxDegree = 5
  ExternalBSplineTolerance = 0.0001
  FullyConstrained = true
  InternalTolerance = 1e-06
  InvalidShape = false
  MakeInternals = false
  MapMode = 5
  Placement = pos=(0,0,0) rot=(1,0,0;1.5708rad)
  Support = -> [XZ_Plane087]
  TreeRank = 1085
  ValidateShape = false
  sketch-geometry (4):
    g0: LineSegment StartX=-30 StartY=-5 StartZ=0 EndX=-44 EndY=-5 EndZ=0
    g1: LineSegment StartX=-44 StartY=-5 StartZ=0 EndX=-44 EndY=10 EndZ=0
    g2: LineSegment StartX=-44 StartY=10 StartZ=0 EndX=-30 EndY=10 EndZ=0
    g3: LineSegment StartX=-30 StartY=10 StartZ=0 EndX=-30 EndY=-5 EndZ=0
  constraints (12):
    c: Coincident(g0,g1)
    c: Coincident(g1,g2)
    c: Coincident(g2,g3)
    c: Coincident(g3,g0)
    c: Horizontal(g0)
    c: Horizontal(g2)
    c: Vertical(g1)
    c: Vertical(g3)
    c: DistanceX(g0) = -30
    c: DistanceX(g2,g2) = 14
    c: DistanceY(g-1,g2) = 10
    c: DistanceY(g0,g-1) = 5
FEATURE [PartDesign::Pocket] Pocket072
  AddSubType = 1
  AlongSketchNormal = false
  AutoTaperInnerAngle = true
  BaseFeature = -> Chamfer062
  CheckUpToFaceLimits = true
  ClaimChildren = false
  Direction = (0,1,-2e-16)
  Fit = 0
  FitJoin = 0
  InnerFit = 0
  InnerFitJoin = 0
  InvalidShape = false
  Length = 5
  Length2 = 10
  Linearize = true
  NewSolid = false
  Profile = -> Sketch143
  ReferenceAxis = -> Sketch143 [N_Axis]
  Refine = true
  Suppress = false
  TaperInnerAngle = 0
  TaperInnerAngleRev = 0
  TreeRank = 1086
  Type = 0
  ValidateShape = true
  _ProfileBasedVersion = 1
  _Version = 1
FEATURE [PartDesign::Mirrored] Mirrored012
  AddSubType = 0
  BaseFeature = -> Pocket072
  CopyShape = false
  HideBaseFeature = false
  InvalidShape = false
  MirrorPlane = -> Sketch143 [V_Axis]
  NewSolid = false
  OffsetBaseFeature = true
  OriginalSubs = -> [Pocket072]
  Originals = -> [Pocket072]
  ParallelTransform = true
  Refine = true
  SubTransform = true
  Suppress = false
  TreeRank = 1087
  ValidateShape = true
  _Version = 3
FEATURE [PartDesign::Chamfer] Chamfer063
  AddSubType = 0
  Angle = 45
  Base = -> Mirrored012 [Edge63,Edge60,Edge21,Edge58]
  BaseFeature = -> Mirrored012
  ChamferType = 0
  FlipDirection = false
  InvalidShape = false
  NewSolid = false
  Refine = true
  Size = 3
  Size2 = 1
  SupportTransform = false
  Suppress = false
  TreeRank = 1088
  UseAllEdges = false
  ValidateShape = true
FEATURE [PartDesign::Fillet] Fillet049
  AddSubType = 0
  Base = -> Chamfer063 [Edge68,Edge56]
  BaseFeature = -> Chamfer063
  InvalidShape = false
  NewSolid = false
  Radius = 2
  Refine = true
  SupportTransform = false
  Suppress = false
  TreeRank = 1089
  UseAllEdges = false
  ValidateShape = true
FEATURE [PartDesign::Body] Body054  label="PareBuffle"
  AutoGroupSolids = false
  ClaimAllChildren = false
  ExportMode = 0
  Group = -> [Sketch140,Pad070,Sketch141,Pocket070,Sketch142,Pocket071,Mirrored011,Chamfer060,Chamfer061,Chamfer062,Sketch143,Pocket072,Mirrored012,Chamfer063,Fillet049]
  InvalidShape = false
  Origin = -> Origin104
  Placement = pos=(0,120,0) rot=(0,0,1;0rad)
  Tip = -> Fillet049
  TreeRank = 1073
  ValidateShape = false
  _ExportChildren = -> [Pad070,Pocket070,Pocket071,Mirrored011,Chamfer060,Chamfer061,Chamfer062,Pocket072,Mirrored012,Chamfer063,Fillet049]
  _GroupVersion = 1
FEATURE [PartDesign::FeatureBase] Clone002
  BaseFeature = -> Chamfer062
  InvalidShape = false
  NewSolid = false
  Suppress = false
  TreeRank = 1465
  ValidateShape = true
FEATURE [Sketcher::SketchObject] Sketch252
  ArcFitTolerance = 1e-06
  AttachmentSupport = -> [Clone002]
  ExternalBSplineMaxDegree = 5
  ExternalBSplineTolerance = 0.0001
  ExternalGeometry = -> [Clone002]
  FullyConstrained = true
  InternalTolerance = 1e-06
  InvalidShape = false
  MakeInternals = true
  MapMode = 5
  Placement = pos=(1.4e-15,-1.1e-15,-5) rot=(1,0,0;3.14159rad)
  Support = -> [Clone002]
  TreeRank = 1467
  ValidateShape = false
  sketch-geometry (6):
    g0: Circle [constr] CenterX=40 CenterY=-10.5 CenterZ=0 NormalX=0 NormalY=0 NormalZ=1 AngleXU=0 Radius=7.5
    g1: Circle [constr] CenterX=40 CenterY=-10.5 CenterZ=0 NormalX=0 NormalY=0 NormalZ=1 AngleXU=0 Radius=6.5
    g2: ArcOfCircle CenterX=40 CenterY=-10.5 CenterZ=0 NormalX=0 NormalY=0 NormalZ=1 AngleXU=0 Radius=6 StartAngle=4.18879 EndAngle=7.21048
    g3: LineSegment StartX=43.6 StartY=-5.7 StartZ=0 EndX=40 EndY=-3 EndZ=0
    g4: LineSegment StartX=37 StartY=-15.6962 StartZ=0 EndX=15.0096 EndY=-3 EndZ=0
    g5: LineSegment StartX=15.0096 StartY=-3 StartZ=0 EndX=40 EndY=-3 EndZ=0
  constraints (14):
    c: Tangent(g0,g-3)
    c: Diameter(g0) = 15
    c: Coincident(g1,g0)
    c: Diameter(g1) = 13
    c: Vertical(g0,g-3)
    c: Coincident(g2,g0)
    c: Coincident(g3,g-3)
    c: PointOnObject(g4,g-3)
    c: Coincident(g5,g4)
    c: Coincident(g5,g3)
    c: Tangent(g4,g2) = 1.5708
    c: Tangent(g3,g2) = -1.5708
    c: Radius(g2) = 6
    c: Angle(g4,g5) = 0.523599
FEATURE [PartDesign::Pad] Pad131
  AddSubType = 0
  AlongSketchNormal = false
  AutoTaperInnerAngle = true
  BaseFeature = -> Clone002
  CheckUpToFaceLimits = true
  ClaimChildren = false
  Direction = (3e-16,-2e-16,-1)
  Fit = 0
  FitJoin = 0
  InnerFit = 0
  InnerFitJoin = 0
  InvalidShape = false
  Length = 25
  Length2 = 10
  Linearize = true
  NewSolid = false
  Profile = -> Sketch252
  ReferenceAxis = -> Sketch252 [N_Axis]
  Refine = true
  Reversed = true
  Suppress = false
  TaperInnerAngle = 0
  TaperInnerAngleRev = 0
  TreeRank = 1468
  Type = 0
  ValidateShape = true
  _ProfileBasedVersion = 1
FEATURE [PartDesign::Draft] Draft003
  AddSubType = 0
  Angle = 50
  Base = -> Pad131 [Face16]
  BaseFeature = -> Pad131
  InvalidShape = false
  NeutralPlane = -> Pad131 [Face10]
  NewSolid = false
  Refine = true
  SupportTransform = false
  Suppress = false
  TreeRank = 1469
  ValidateShape = true
FEATURE [PartDesign::Fillet] Fillet089
  AddSubType = 0
  Base = -> Draft003 [Edge30]
  BaseFeature = -> Draft003
  InvalidShape = false
  NewSolid = false
  Radius = 20
  Refine = true
  SupportTransform = false
  Suppress = false
  TreeRank = 1470
  UseAllEdges = false
  ValidateShape = true
FEATURE [Sketcher::SketchObject] Sketch253
  ArcFitTolerance = 1e-06
  AttachmentSupport = -> [Fillet089]
  ExternalBSplineMaxDegree = 5
  ExternalBSplineTolerance = 0.0001
  ExternalGeometry = -> [Fillet089]
  FullyConstrained = true
  InternalTolerance = 1e-06
  InvalidShape = false
  MakeInternals = true
  MapMode = 5
  Placement = pos=(1.4e-15,-1.4e-15,-5) rot=(1,0,0;3.14159rad)
  Support = -> [Fillet089]
  TreeRank = 1471
  ValidateShape = false
  sketch-geometry (1):
    g0: Circle CenterX=40 CenterY=-10.5 CenterZ=0 NormalX=0 NormalY=0 NormalZ=1 AngleXU=0 Radius=1.6
  constraints (2):
    c: Coincident(g0,g-3)
    c: Diameter(g0) = 3.2
FEATURE [PartDesign::Pocket] Pocket084
  AddSubType = 1
  AlongSketchNormal = false
  AutoTaperInnerAngle = true
  BaseFeature = -> Fillet089
  CheckUpToFaceLimits = true
  ClaimChildren = false
  Direction = (-3e-16,3e-16,1)
  Fit = 0
  FitJoin = 0
  InnerFit = 0
  InnerFitJoin = 0
  InvalidShape = false
  Length = 28
  Length2 = 10
  Linearize = true
  NewSolid = false
  Profile = -> Sketch253
  ReferenceAxis = -> Sketch253 [N_Axis]
  Refine = true
  Suppress = false
  TaperInnerAngle = 0
  TaperInnerAngleRev = 0
  TreeRank = 1472
  Type = 0
  ValidateShape = true
  _ProfileBasedVersion = 1
  _Version = 1
FEATURE [Sketcher::SketchObject] Sketch254
  ArcFitTolerance = 1e-06
  AttachmentOffset = pos=(0,0,-6) rot=(0,0,1;0rad)
  AttachmentSupport = -> [Pocket084]
  ExternalBSplineMaxDegree = 5
  ExternalBSplineTolerance = 0.0001
  ExternalGeometry = -> [Pocket084]
  FullyConstrained = true
  InternalTolerance = 1e-06
  InvalidShape = false
  MakeInternals = true
  MapMode = 5
  Placement = pos=(-3e-16,3e-16,1) rot=(1,0,0;3.14159rad)
  Support = -> [Pocket084]
  TreeRank = 1473
  ValidateShape = false
  sketch-geometry (1):
    g0: Circle CenterX=40 CenterY=-10.5 CenterZ=0 NormalX=0 NormalY=0 NormalZ=1 AngleXU=0 Radius=7.5
  constraints (2):
    c: Coincident(g0,g-3)
    c: Diameter(g0) = 15
FEATURE [PartDesign::Pocket] Pocket085
  AddSubType = 1
  AlongSketchNormal = false
  AutoTaperInnerAngle = true
  BaseFeature = -> Pocket084
  CheckUpToFaceLimits = true
  ClaimChildren = false
  Direction = (-3e-16,3e-16,1)
  Fit = 0
  FitJoin = 0
  InnerFit = 0
  InnerFitJoin = 0
  InvalidShape = false
  Length = 33
  Length2 = 10
  Linearize = true
  NewSolid = false
  Profile = -> Sketch254
  ReferenceAxis = -> Sketch254 [N_Axis]
  Refine = true
  Suppress = false
  TaperInnerAngle = 0
  TaperInnerAngleRev = 0
  TreeRank = 1474
  Type = 0
  ValidateShape = true
  _ProfileBasedVersion = 1
  _Version = 1
FEATURE [PartDesign::Fillet] Fillet090
  AddSubType = 0
  Base = -> Pocket085 [Edge71]
  BaseFeature = -> Pocket085
  InvalidShape = false
  NewSolid = false
  Radius = 3
  Refine = true
  SupportTransform = false
  Suppress = false
  TreeRank = 1475
  UseAllEdges = false
  ValidateShape = true
FEATURE [Sketcher::SketchObject] Sketch255
  ArcFitTolerance = 1e-06
  AttachmentSupport = -> [Fillet090]
  ExternalBSplineMaxDegree = 5
  ExternalBSplineTolerance = 0.0001
  ExternalGeometry = -> [Fillet090]
  FullyConstrained = true
  InternalTolerance = 1e-06
  InvalidShape = false
  MakeInternals = true
  MapMode = 5
  Placement = pos=(-3e-16,3e-16,1) rot=(0,0,1;0rad)
  Support = -> [Fillet090]
  TreeRank = 1476
  ValidateShape = false
  sketch-geometry (2):
    g0: Circle CenterX=40 CenterY=10.5 CenterZ=0 NormalX=0 NormalY=0 NormalZ=1 AngleXU=0 Radius=1.6
    g1: Circle CenterX=40 CenterY=10.5 CenterZ=0 NormalX=0 NormalY=0 NormalZ=1 AngleXU=0 Radius=4
  constraints (4):
    c: Coincident(g0,g-3)
    c: Coincident(g1,g0)
    c: Equal(g0,g-3)
    c: Diameter(g1) = 8
FEATURE [PartDesign::Pad] Pad132
  AddSubType = 0
  AlongSketchNormal = false
  AutoTaperInnerAngle = true
  BaseFeature = -> Fillet090
  CheckUpToFaceLimits = true
  ClaimChildren = false
  Direction = (-3e-16,3e-16,1)
  Fit = 0
  FitJoin = 0
  InnerFit = 0
  InnerFitJoin = 0
  InvalidShape = false
  Length = 1
  Length2 = 10
  Linearize = true
  NewSolid = false
  Profile = -> Sketch255
  ReferenceAxis = -> Sketch255 [N_Axis]
  Refine = true
  Suppress = false
  TaperInnerAngle = 0
  TaperInnerAngleRev = 0
  TreeRank = 1477
  Type = 0
  ValidateShape = true
  _ProfileBasedVersion = 1
FEATURE [PartDesign::Chamfer] Chamfer091
  AddSubType = 0
  Angle = 45
  Base = -> Pad132 [Edge82]
  BaseFeature = -> Pad132
  ChamferType = 1
  FlipDirection = false
  InvalidShape = false
  NewSolid = false
  Refine = true
  Size = 0.99
  Size2 = 1
  SupportTransform = false
  Suppress = false
  TreeRank = 1478
  UseAllEdges = false
  ValidateShape = true
FEATURE [PartDesign::Chamfer] Chamfer092
  AddSubType = 0
  Angle = 45
  Base = -> Chamfer091 [Edge6]
  BaseFeature = -> Chamfer091
  ChamferType = 0
  FlipDirection = false
  InvalidShape = false
  NewSolid = false
  Refine = true
  Size = 0.5
  Size2 = 1
  SupportTransform = false
  Suppress = false
  TreeRank = 1479
  UseAllEdges = false
  ValidateShape = true
FEATURE [Sketcher::SketchObject] Sketch256
  ArcFitTolerance = 1e-06
  AttachmentSupport = -> [Chamfer092]
  ExternalBSplineMaxDegree = 5
  ExternalBSplineTolerance = 0.0001
  ExternalGeometry = -> [Chamfer092]
  FullyConstrained = true
  InternalTolerance = 1e-06
  InvalidShape = false
  MakeInternals = true
  MapMode = 5
  Placement = pos=(1.4e-15,-1.4e-15,-5) rot=(1,0,0;3.14159rad)
  Support = -> [Chamfer092]
  TreeRank = 1480
  ValidateShape = false
  sketch-geometry (7):
    g0: LineSegment StartX=43.2332 StartY=-10.5 StartZ=0 EndX=41.6166 EndY=-7.7 EndZ=0
    g1: LineSegment StartX=41.6166 StartY=-7.7 StartZ=0 EndX=38.3834 EndY=-7.7 EndZ=0
    g2: LineSegment StartX=38.3834 StartY=-7.7 StartZ=0 EndX=36.7668 EndY=-10.5 EndZ=0
    g3: LineSegment StartX=36.7668 StartY=-10.5 StartZ=0 EndX=38.3834 EndY=-13.3 EndZ=0
    g4: LineSegment StartX=38.3834 StartY=-13.3 StartZ=0 EndX=41.6166 EndY=-13.3 EndZ=0
    g5: LineSegment StartX=41.6166 StartY=-13.3 StartZ=0 EndX=43.2332 EndY=-10.5 EndZ=0
    g6: Circle [constr] CenterX=40 CenterY=-10.5 CenterZ=0 NormalX=0 NormalY=0 NormalZ=1 AngleXU=0 Radius=3.23316
  constraints (16):
    c: Coincident(g0,g1)
    c: Coincident(g1,g2)
    c: Coincident(g2,g3)
    c: Coincident(g3,g4)
    c: Coincident(g4,g5)
    c: Coincident(g5,g0)
    c: Equal(g0, g1-g5) x5
    c: PointOnObject(g0,g6)
    c: PointOnObject(g1,g6)
    c: PointOnObject(g2,g6)
    c: PointOnObject(g3,g6)
    c: PointOnObject(g4,g6)
    c: PointOnObject(g5,g6)
    c: Coincident(g6,g-3)
    c: Horizontal(g1)
    c: DistanceY(g4,g0) = 5.6
FEATURE [PartDesign::Pocket] Pocket086
  AddSubType = 1
  AlongSketchNormal = false
  AutoTaperInnerAngle = true
  BaseFeature = -> Chamfer092
  CheckUpToFaceLimits = true
  ClaimChildren = false
  Direction = (-3e-16,3e-16,1)
  Fit = 0
  FitJoin = 0
  InnerFit = 0
  InnerFitJoin = 0
  InvalidShape = false
  Length = 4
  Length2 = 10
  Linearize = true
  NewSolid = false
  Profile = -> Sketch256
  ReferenceAxis = -> Sketch256 [N_Axis]
  Refine = true
  Suppress = false
  TaperInnerAngle = 0
  TaperInnerAngleRev = 0
  TreeRank = 1481
  Type = 0
  ValidateShape = true
  _ProfileBasedVersion = 1
  _Version = 1
FEATURE [PartDesign::Chamfer] Chamfer093
  AddSubType = 0
  Angle = 45
  Base = -> Pocket086 [Edge40,Edge39,Edge44,Edge43,Edge42,Edge41]
  BaseFeature = -> Pocket086
  ChamferType = 0
  FlipDirection = false
  InvalidShape = false
  NewSolid = false
  Refine = true
  Size = 0.4
  Size2 = 1
  SupportTransform = false
  Suppress = false
  TreeRank = 1482
  UseAllEdges = false
  ValidateShape = true
FEATURE [PartDesign::Mirrored] Mirrored019
  AddSubType = 0
  BaseFeature = -> Chamfer093
  CopyShape = false
  HideBaseFeature = false
  InvalidShape = false
  MirrorPlane = -> Sketch252 [V_Axis]
  NewSolid = false
  OffsetBaseFeature = true
  OriginalSubs = -> [Pad131,Draft003,Fillet089,Pocket084,Pocket085,Fillet090,Pad132,Chamfer091,Chamfer092,Pocket086,Chamfer093]
  Originals = -> [Pad131,Draft003,Fillet089,Pocket084,Pocket085,Fillet090,Pad132,Chamfer091,Chamfer092,Pocket086,Chamfer093]
  ParallelTransform = true
  Refine = true
  SubTransform = true
  Suppress = false
  TreeRank = 1483
  ValidateShape = true
  _Version = 4
FEATURE [PartDesign::Body] Body108  label="PareBuffleRoulement"
  AutoGroupSolids = false
  BaseFeature = -> Chamfer062
  ClaimAllChildren = false
  ExportMode = 0
  Group = -> [Clone002,Sketch252,Pad131,Draft003,Fillet089,Sketch253,Pocket084,Sketch254,Pocket085,Fillet090,Sketch255,Pad132,Chamfer091,Chamfer092,Sketch256,Pocket086,Chamfer093,Mirrored019]
  InvalidShape = false
  Origin = -> Origin217
  Placement = pos=(0,120,0) rot=(0,0,1;0rad)
  Tip = -> Mirrored019
  TreeRank = 1466
  ValidateShape = false
  _ExportChildren = -> [Clone002,Pad131,Draft003,Fillet089,Pocket084,Pocket085,Fillet090,Pad132,Chamfer091,Chamfer092,Pocket086,Chamfer093,Mirrored019]
  _GroupVersion = 1
FEATURE [Part::SubShapeBinder] Import015  label="Import015(Chamfer058)"
  BindCopyOnChange = 0
  BindMode = 0
  ClaimChildren = false
  Context = -> <external ../holonomic-base.FCStd>#Link004 [Body109.Import015.]
  EdgeTolerance = 1e-06
  FillStyle = 0
  Fuse = false
  InvalidShape = false
  MakeFace = false
  MergeEdges = true
  OffsetFill = false
  OffsetIntersection = false
  OffsetJoinType = 0
  OffsetOpenResult = false
  Outline = false
  PartialLoad = false
  Relative = true
  SplitEdges = false
  Support = -> [Body052[Chamfer058.]]
  TightBound = false
  TreeRank = 1516
  ValidateShape = false
  _Version = 8
FEATURE [Sketcher::SketchObject] Sketch257
  ArcFitTolerance = 1e-06
  AttachmentSupport = -> [Import015]
  ExternalBSplineMaxDegree = 5
  ExternalBSplineTolerance = 0.0001
  ExternalGeometry = -> [Import015]
  FullyConstrained = true
  InternalTolerance = 1e-06
  InvalidShape = false
  MakeInternals = false
  MapMode = 5
  Placement = pos=(-43,0,-9.5e-15) rot=(0.57735,-0.57735,-0.57735;2.0944rad)
  Support = -> [Import015]
  TreeRank = 1517
  ValidateShape = false
  sketch-geometry (8):
    g0: Circle CenterX=-54.5823 CenterY=296.171 CenterZ=0 NormalX=0 NormalY=0 NormalZ=1 AngleXU=0 Radius=1.65
    g1: ArcOfCircle CenterX=-54.5823 CenterY=296.171 CenterZ=0 NormalX=0 NormalY=0 NormalZ=1 AngleXU=0 Radius=6 StartAngle=1.3e-15 EndAngle=3.14159
    g2: ArcOfCircle CenterX=-54.5823 CenterY=286.171 CenterZ=0 NormalX=0 NormalY=0 NormalZ=1 AngleXU=0 Radius=6 StartAngle=3.14159 EndAngle=6.28319
    g3: LineSegment StartX=-60.5823 StartY=296.171 StartZ=0 EndX=-60.5823 EndY=286.171 EndZ=0
    g4: LineSegment StartX=-48.5823 StartY=286.171 StartZ=0 EndX=-48.5823 EndY=296.171 EndZ=0
    g5: LineSegment [constr] StartX=-69.1647 StartY=298.743 StartZ=0 EndX=-40 EndY=293.6 EndZ=0
    g6: Circle [constr] CenterX=-54.5823 CenterY=286.171 CenterZ=0 NormalX=0 NormalY=0 NormalZ=1 AngleXU=0 Radius=6
    g7: Circle [constr] CenterX=-54.5823 CenterY=296.171 CenterZ=0 NormalX=0 NormalY=0 NormalZ=1 AngleXU=0 Radius=4
  constraints (19):
    c: Diameter(g0) = 3.3
    c: Tangent(g1,g3) = -1.5708
    c: Tangent(g3,g2) = -1.5708
    c: Tangent(g2,g4) = -1.5708
    c: Tangent(g4,g1) = -1.5708
    c: Equal(g1,g2)
    c: Coincident(g1,g0)
    c: Vertical(g3)
    c: Radius(g1) = 6
    c: PointOnObject(g5,g-4)
    c: PointOnObject(g5,g-3)
    c: Perpendicular(g-4,g5)
    c: Symmetric(g5,g5,g0)
    c: DistanceY(g5,g-3) = 5
    c: Coincident(g6,g2)
    c: PointOnObject(g2,g6)
    c: Coincident(g7,g0)
    c: Tangent(g7,g6)
    c: Diameter(g7) = 8
FEATURE [PartDesign::Pad] Pad133
  AddSubType = 0
  AlongSketchNormal = false
  AutoTaperInnerAngle = true
  CheckUpToFaceLimits = true
  ClaimChildren = false
  Direction = (-1,1e-16,-1e-16)
  Fit = 0
  FitJoin = 0
  InnerFit = 0
  InnerFitJoin = 0
  InvalidShape = false
  Length = 7
  Length2 = 10
  Linearize = true
  NewSolid = false
  Profile = -> Sketch257
  ReferenceAxis = -> Sketch257 [N_Axis]
  Refine = true
  Suppress = false
  TaperInnerAngle = 0
  TaperInnerAngleRev = 0
  TreeRank = 1518
  Type = 0
  ValidateShape = true
  _ProfileBasedVersion = 1
FEATURE [Sketcher::SketchObject] Sketch258
  ArcFitTolerance = 1e-06
  AttachmentSupport = -> [Pad133]
  ExternalBSplineMaxDegree = 5
  ExternalBSplineTolerance = 0.0001
  ExternalGeometry = -> [Pad133]
  FullyConstrained = true
  InternalTolerance = 1e-06
  InvalidShape = false
  MakeInternals = false
  MapMode = 5
  Placement = pos=(-43,0,0) rot=(0.57735,0.57735,0.57735;2.0944rad)
  Support = -> [Pad133]
  TreeRank = 1519
  ValidateShape = false
  sketch-geometry (7):
    g0: LineSegment StartX=57.8155 StartY=286.171 StartZ=0 EndX=56.1989 EndY=288.971 EndZ=0
    g1: LineSegment StartX=56.1989 StartY=288.971 StartZ=0 EndX=52.9658 EndY=288.971 EndZ=0
    g2: LineSegment StartX=52.9658 StartY=288.971 StartZ=0 EndX=51.3492 EndY=286.171 EndZ=0
    g3: LineSegment StartX=51.3492 StartY=286.171 StartZ=0 EndX=52.9658 EndY=283.371 EndZ=0
    g4: LineSegment StartX=52.9658 StartY=283.371 StartZ=0 EndX=56.1989 EndY=283.371 EndZ=0
    g5: LineSegment StartX=56.1989 StartY=283.371 StartZ=0 EndX=57.8155 EndY=286.171 EndZ=0
    g6: Circle [constr] CenterX=54.5823 CenterY=286.171 CenterZ=0 NormalX=0 NormalY=0 NormalZ=1 AngleXU=0 Radius=3.23316
  constraints (16):
    c: Coincident(g0,g1)
    c: Coincident(g1,g2)
    c: Coincident(g2,g3)
    c: Coincident(g3,g4)
    c: Coincident(g4,g5)
    c: Coincident(g5,g0)
    c: Equal(g0, g1-g5) x5
    c: PointOnObject(g0,g6)
    c: PointOnObject(g1,g6)
    c: PointOnObject(g2,g6)
    c: PointOnObject(g3,g6)
    c: PointOnObject(g4,g6)
    c: PointOnObject(g5,g6)
    c: Coincident(g6,g-3)
    c: Horizontal(g1)
    c: DistanceY(g4,g0) = 5.6
FEATURE [PartDesign::Pocket] Pocket087
  AddSubType = 1
  AlongSketchNormal = false
  AutoTaperInnerAngle = true
  BaseFeature = -> Pad133
  CheckUpToFaceLimits = true
  ClaimChildren = false
  Direction = (-1,0,0)
  Fit = 0
  FitJoin = 0
  InnerFit = 0
  InnerFitJoin = 0
  InvalidShape = false
  Length = 5
  Length2 = 10
  Linearize = true
  NewSolid = false
  Profile = -> Sketch258
  ReferenceAxis = -> Sketch258 [N_Axis]
  Refine = true
  Suppress = false
  TaperInnerAngle = 0
  TaperInnerAngleRev = 0
  TreeRank = 1520
  Type = 0
  ValidateShape = true
  _ProfileBasedVersion = 1
  _Version = 1
FEATURE [Sketcher::SketchObject] Sketch259
  ArcFitTolerance = 1e-06
  AttachmentSupport = -> [Pocket087]
  ExternalBSplineMaxDegree = 5
  ExternalBSplineTolerance = 0.0001
  ExternalGeometry = -> [Pocket087]
  FullyConstrained = true
  InternalTolerance = 1e-06
  InvalidShape = false
  MakeInternals = false
  MapMode = 5
  Placement = pos=(-50,0,0) rot=(0.57735,-0.57735,-0.57735;2.0944rad)
  Support = -> [Pocket087]
  TreeRank = 1521
  ValidateShape = false
  sketch-geometry (1):
    g0: Circle CenterX=-54.5823 CenterY=286.171 CenterZ=0 NormalX=0 NormalY=0 NormalZ=1 AngleXU=0 Radius=1.65
  constraints (2):
    c: Coincident(g0,g-3)
    c: Equal(g0,g-4)
FEATURE [PartDesign::Pocket] Pocket088
  AddSubType = 1
  AlongSketchNormal = false
  AutoTaperInnerAngle = true
  BaseFeature = -> Pocket087
  CheckUpToFaceLimits = true
  ClaimChildren = false
  Direction = (1,0,0)
  Fit = 0
  FitJoin = 0
  InnerFit = 0
  InnerFitJoin = 0
  InvalidShape = false
  Length = 5
  Length2 = 10
  Linearize = true
  NewSolid = false
  Profile = -> Sketch259
  ReferenceAxis = -> Sketch259 [N_Axis]
  Refine = true
  Suppress = false
  TaperInnerAngle = 0
  TaperInnerAngleRev = 0
  TreeRank = 1522
  Type = 0
  ValidateShape = true
  _ProfileBasedVersion = 1
  _Version = 1
FEATURE [PartDesign::Chamfer] Chamfer094
  AddSubType = 0
  Angle = 45
  Base = -> Pocket088 [Edge20]
  BaseFeature = -> Pocket088
  ChamferType = 0
  FlipDirection = false
  InvalidShape = false
  NewSolid = false
  Refine = true
  Size = 1.5
  Size2 = 1
  SupportTransform = false
  Suppress = false
  TreeRank = 1523
  UseAllEdges = false
  ValidateShape = true
FEATURE [PartDesign::Chamfer] Chamfer095
  AddSubType = 0
  Angle = 45
  Base = -> Chamfer094 [Edge5,Edge16,Edge20,Edge25,Edge24,Edge22,Edge21,Edge26,Edge23,Edge18,Edge6]
  BaseFeature = -> Chamfer094
  ChamferType = 0
  FlipDirection = false
  InvalidShape = false
  NewSolid = false
  Refine = true
  Size = 0.4
  Size2 = 1
  SupportTransform = false
  Suppress = false
  TreeRank = 1524
  UseAllEdges = false
  ValidateShape = true
FEATURE [PartDesign::Body] Body109  label="TendeurElastique"
  AutoGroupSolids = false
  ClaimAllChildren = false
  ExportMode = 0
  Group = -> [Import015,Sketch257,Pad133,Sketch258,Pocket087,Sketch259,Pocket088,Chamfer094,Chamfer095]
  InvalidShape = false
  Origin = -> Origin218
  Tip = -> Chamfer095
  TreeRank = 1515
  ValidateShape = false
  _ExportChildren = -> [Import015,Pad133,Pocket087,Pocket088,Chamfer094,Chamfer095]
  _GroupVersion = 1
COMPONENT P2 — geometry summary ("Main_Board_Assembled"; no construction recipe available for this part):
  bounding box: 167.9 x 80.0 x 49.0 mm
  tessellated surface: 15,768 triangles
  volume: 46836 mm^3 (7% of its bounding box)
  symmetry: mirror-symmetric across its x mid-plane
COMPONENT P3 — geometry summary ("XBee_Assembled"; no construction recipe available for this part):
  bounding box: 80.0 x 51.4 x 24.0 mm
  tessellated surface: 16,216 triangles
  volume: 24272 mm^3 (25% of its bounding box)
  symmetry: mirror-symmetric across its x mid-plane
COMPONENT P4 — geometry summary ("Battery_Assembled"; no construction recipe available for this part):
  bounding box: 138.2 x 107.4 x 80.0 mm
  tessellated surface: 36,056 triangles
  volume: 117746 mm^3 (10% of its bounding box)
  symmetry: mirror-symmetric across its x mid-plane
COMPONENT P5 — geometry summary ("DriverBoard_Assembled"; no construction recipe available for this part):
  bounding box: 80.0 x 51.5 x 45.6 mm
  tessellated surface: 12,082 triangles
  volume: 34583 mm^3 (18% of its bounding box)
COMPONENT P6 — geometry summary ("Ihm_Assembled"; no construction recipe available for this part):
  bounding box: 80.0 x 53.7 x 34.9 mm
  tessellated surface: 27,708 triangles
  volume: 22587 mm^3 (15% of its bounding box)
COMPONENT P7 — geometry summary ("Screen-Assembled"; no construction recipe available for this part):
  bounding box: 178.9 x 80.0 x 71.7 mm
  tessellated surface: 22,640 triangles
  volume: 29196 mm^3 (3% of its bounding box)
COMPONENT P8 — geometry summary ("BAU_Assembled"; no construction recipe available for this part):
  bounding box: 80.0 x 53.7 x 24.3 mm
  tessellated surface: 11,254 triangles
  volume: 11821 mm^3 (11% of its bounding box)
COMPONENT P9 — geometry summary ("Servo_Assembled"; no construction recipe available for this part):
  bounding box: 80.0 x 30.1 x 12.9 mm
  tessellated surface: 1,812 triangles
  volume: 6711 mm^3 (22% of its bounding box)
COMPONENT P10 — geometry summary ("PCA9685_Assembled"; no construction recipe available for this part):
  bounding box: 80.0 x 37.9 x 13.6 mm
  tessellated surface: 2,044 triangles
  volume: 8747 mm^3 (21% of its bounding box)
COMPONENT P11 — geometry summary ("Pump_Assembled"; no construction recipe available for this part):
  bounding box: 80.0 x 69.5 x 15.1 mm
  tessellated surface: 2,564 triangles
  volume: 16127 mm^3 (19% of its bounding box)
  symmetry: 2-fold rotationally symmetric about the x axis; mirror-symmetric across its x mid-plane
COMPONENT P12 — geometry summary ("Cache10mm_Assembled"; no construction recipe available for this part):
  bounding box: 80.0 x 54.0 x 10.4 mm
  tessellated surface: 812 triangles
  volume: 10666 mm^3 (24% of its bounding box)
  symmetry: mirror-symmetric across its x mid-plane
COMPONENT P13 — geometry summary ("TopBattery_Assembled"; no construction recipe available for this part):
  bounding box: 80.0 x 47.8 x 21.1 mm
  tessellated surface: 4,692 triangles
  volume: 18598 mm^3 (23% of its bounding box)
  symmetry: mirror-symmetric across its x mid-plane
COMPONENT P14 — geometry summary ("CacheCable_Assembled"; no construction recipe available for this part):
  bounding box: 80.0 x 29.9 x 22.4 mm
  tessellated surface: 23,838 triangles
  volume: 7880 mm^3 (15% of its bounding box)
  symmetry: mirror-symmetric across its x mid-plane
COMPONENT P15 — recipe-attached ("633ZZ", modeled in this document).
Construction recipe (the document's own serialized feature program — sketch geometry with constraints, then the solid features built on it; lengths are millimeters unless a unit is written):

FEATURE [Sketcher::SketchObject] Sketch169
  ArcFitTolerance = 0
  ExternalBSplineMaxDegree = 0
  ExternalBSplineTolerance = 0
  FixShape = 1
  FullyConstrained = true
  InternalTolerance = 1e-06
  InvalidShape = false
  MakeInternals = false
  MapMode = 5
  Placement = pos=(0,0,0) rot=(1,0,0;1.5708rad)
  TreeRank = 0
  ValidateShape = false
  sketch-geometry (12):
    g0: LineSegment StartX=-5.5 StartY=1.2718e-12 StartZ=0 EndX=-6.5 EndY=1.052e-12 EndZ=0
    g1: LineSegment StartX=-6.5 StartY=1.052e-12 StartZ=0 EndX=-6.5 EndY=5 EndZ=0
    g2: LineSegment StartX=-6.5 StartY=5 StartZ=0 EndX=-5.5 EndY=5 EndZ=0
    g3: LineSegment StartX=-5.5 StartY=5 StartZ=0 EndX=-5.5 EndY=4.6 EndZ=0
    g4: LineSegment StartX=-5.5 StartY=4.6 StartZ=0 EndX=-2.5 EndY=4.6 EndZ=0
    g5: LineSegment StartX=-2.5 StartY=4.6 StartZ=0 EndX=-2.5 EndY=5 EndZ=0
    g6: LineSegment StartX=-2.5 StartY=5 StartZ=0 EndX=-1.5 EndY=5 EndZ=0
    g7: LineSegment StartX=-1.5 StartY=5 StartZ=0 EndX=-1.5 EndY=0 EndZ=0
    g8: LineSegment StartX=-1.5 StartY=0 StartZ=0 EndX=-2.5 EndY=0 EndZ=0
    g9: LineSegment StartX=-2.5 StartY=0 StartZ=0 EndX=-2.5 EndY=0.4 EndZ=0
    g10: LineSegment StartX=-2.5 StartY=0.4 StartZ=0 EndX=-5.5 EndY=0.4 EndZ=0
    g11: LineSegment StartX=-5.5 StartY=0.4 StartZ=0 EndX=-5.5 EndY=1.2718e-12 EndZ=0
  constraints (36):
    c: PointOnObject(g0,g-1)
    c: PointOnObject(g0,g-1)
    c: Coincident(g0,g1)
    c: Vertical(g1)
    c: Coincident(g1,g2)
    c: Horizontal(g2)
    c: Coincident(g2,g3)
    c: Vertical(g3)
    c: Coincident(g3,g4)
    c: Horizontal(g4)
    c: Coincident(g4,g5)
    c: Vertical(g5)
    c: Coincident(g5,g6)
    c: Horizontal(g6)
    c: Coincident(g6,g7)
    c: PointOnObject(g7,g-1)
    c: Vertical(g7)
    c: Coincident(g7,g8)
    c: PointOnObject(g8,g-1)
    c: Coincident(g8,g9)
    c: Vertical(g9)
    c: Coincident(g9,g10)
    c: Horizontal(g10)
    c: Coincident(g10,g11)
    c: Coincident(g11,g0)
    c: Vertical(g11)
    c: DistanceX(g7) = -1.5
    c: DistanceX(g0) = -6.5
    c: Equal(g8,g0)
    c: Equal(g2,g6)
    c: Equal(g4,g10)
    c: Equal(g3,g11)
    c: DistanceY(g3,g3) = 0.4
    c: DistanceX(g8,g8) = 1
    c: DistanceY(g1,g1) = 5
    c: PointOnObject(g2,g6)
FEATURE [PartDesign::Revolution] Revolution012
  AddSubType = 0
  Angle = 360
  Axis = (0,0,1)
  Base = (0,0,0)
  ClaimChildren = false
  Fit = 0
  FitJoin = 0
  FixShape = 1
  InnerFit = 0
  InnerFitJoin = 0
  InvalidShape = false
  NewSolid = false
  Placement = pos=(0,0,0) rot=(1,0,0;1.5708rad)
  Profile = -> Sketch169
  ReferenceAxis = -> Sketch169 [V_Axis]
  Refine = true
  Suppress = false
  TreeRank = 0
  ValidateShape = true
  _ProfileBasedVersion = 0
FEATURE [PartDesign::Body] Body080  label="CoreMR149"
  AutoGroupSolids = false
  ClaimAllChildren = false
  ExportMode = 0
  FixShape = 1
  Group = -> [Sketch169,Revolution012]
  InvalidShape = false
  Origin = -> Origin166
  SingleSolid = true
  Tip = -> Revolution012
  TreeRank = 0
  ValidateShape = false
  _ExportChildren = -> [Revolution012]
  _GroupVersion = 1
FEATURE [Sketcher::SketchObject] Sketch170
  ArcFitTolerance = 0
  ExternalBSplineMaxDegree = 0
  ExternalBSplineTolerance = 0
  FixShape = 1
  FullyConstrained = true
  InternalTolerance = 1e-06
  InvalidShape = false
  MakeInternals = false
  MapMode = 5
  Placement = pos=(0,0,0) rot=(1,0,0;1.5708rad)
  TreeRank = 0
  ValidateShape = false
  sketch-geometry (4):
    g0: LineSegment StartX=-5.5 StartY=5 StartZ=0 EndX=-2.5 EndY=5 EndZ=0
    g1: LineSegment StartX=-2.5 StartY=5 StartZ=0 EndX=-2.5 EndY=0 EndZ=0
    g2: LineSegment StartX=-2.5 StartY=3e-16 StartZ=0 EndX=-5.5 EndY=3e-16 EndZ=0
    g3: LineSegment StartX=-5.5 StartY=3e-16 StartZ=0 EndX=-5.5 EndY=5 EndZ=0
  constraints (12):
    c: Coincident(g0,g1)
    c: Coincident(g1,g2)
    c: Coincident(g2,g3)
    c: Coincident(g3,g0)
    c: Horizontal(g0)
    c: Horizontal(g2)
    c: Vertical(g1)
    c: Vertical(g3)
    c: PointOnObject(g1,g-1)
    c: DistanceY(g3,g3) = 5
    c: DistanceX(g1) = -2.5
    c: DistanceX(g2) = -5.5
FEATURE [PartDesign::Revolution] Revolution013
  AddSubType = 0
  Angle = 360
  Axis = (0,0,1)
  Base = (0,0,0)
  ClaimChildren = false
  Fit = 0
  FitJoin = 0
  FixShape = 1
  InnerFit = 0
  InnerFitJoin = 0
  InvalidShape = false
  NewSolid = false
  Placement = pos=(0,0,0) rot=(1,0,0;1.5708rad)
  Profile = -> Sketch170
  ReferenceAxis = -> Sketch170 [V_Axis]
  Refine = true
  Suppress = false
  TreeRank = 0
  ValidateShape = true
  _ProfileBasedVersion = 0
FEATURE [PartDesign::Body] Body081  label="Sleeve001"
  AutoGroupSolids = false
  ClaimAllChildren = false
  ExportMode = 0
  FixShape = 1
  Group = -> [Sketch170,Revolution013]
  InvalidShape = false
  Origin = -> Origin167
  SingleSolid = true
  Tip = -> Revolution013
  TreeRank = 0
  ValidateShape = false
  _ExportChildren = -> [Revolution013]
  _GroupVersion = 1
PROVENANCE & LICENSES
A FreeCAD (.FCStd) document from a public repository crawl; recipes are the document's own serialized feature recipes (and, for linked parts, companion documents' recipes).
License: as declared in the source repository (recorded in the dataset sidecar).
